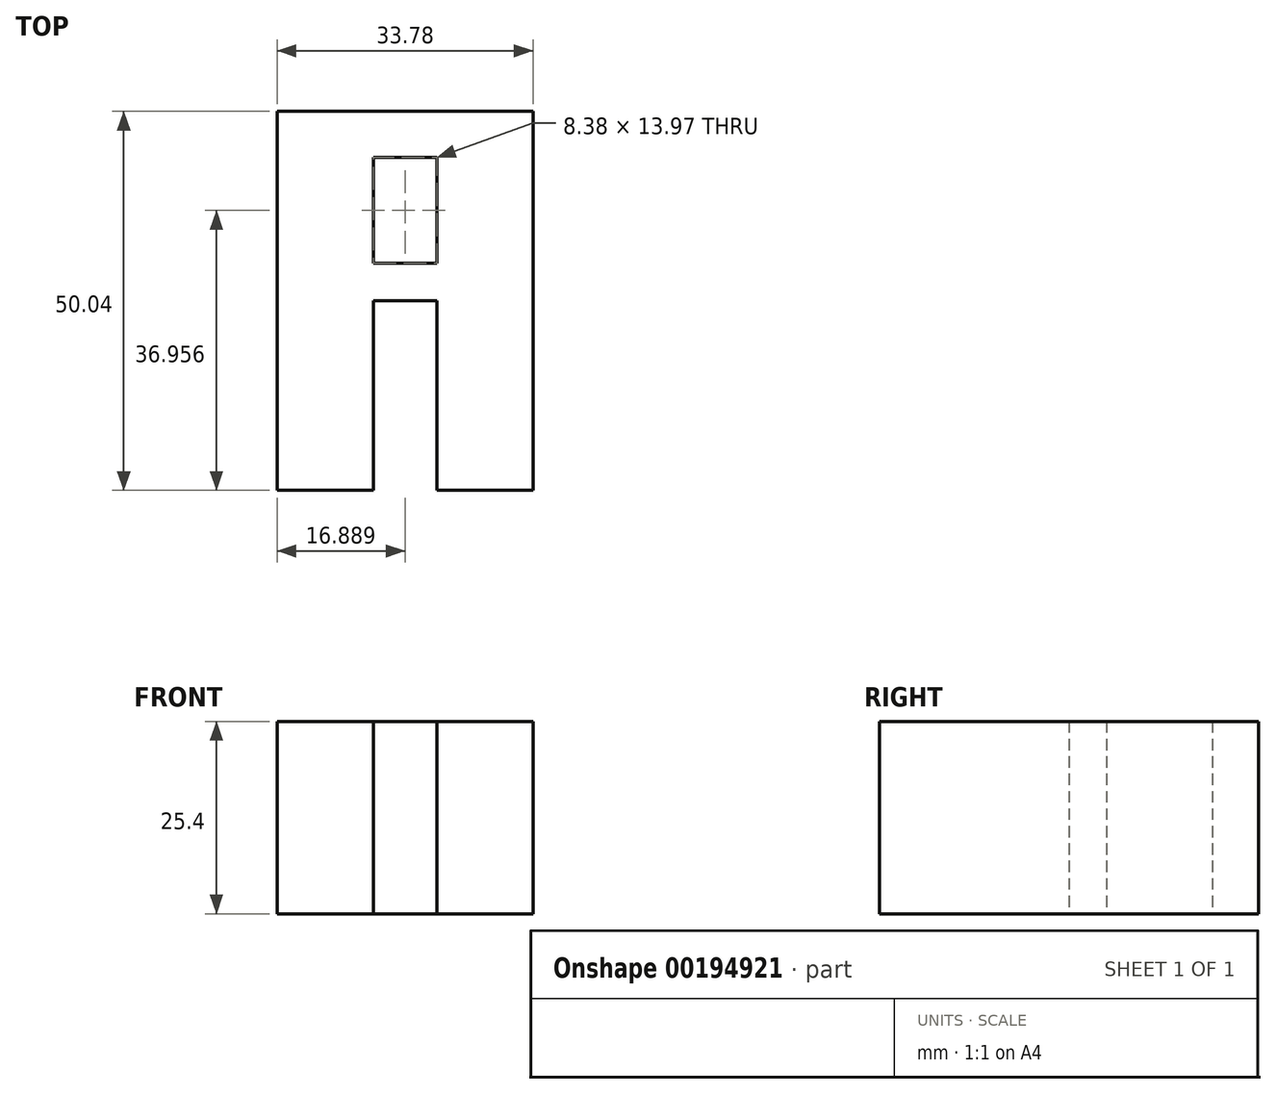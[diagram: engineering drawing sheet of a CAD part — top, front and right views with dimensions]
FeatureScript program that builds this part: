
annotation { "Feature Type Name" : "Feature", "Feature Type Description" : "" }
export const myFeature = defineFeature(function(context is Context, id is Id, definition is map)
    precondition{}
    {
        {
            var Q0;
            Q0=qCreatedBy(makeId("Top.planeOp"),FACE);
            var sketch = newSketch(context, id + "F0", { "sketchPlane" : qUnion([Q0])});
            skLineSegment(sketch, "E0.bottom", {"start": v(-24.9, 25.53) * mm, "end": v(-12.2, 25.53) * mm});
            skLineSegment(sketch, "E0.top", {"start": v(-24.9, -24.51) * mm, "end": v(-12.2, -24.51) * mm});
            skLineSegment(sketch, "E0.left", {"start": v(-24.9, 25.53) * mm, "end": v(-24.9, -24.51) * mm});
            skLineSegment(sketch, "E0.right", {"start": v(-12.2, 19.43) * mm, "end": v(-12.2, 5.46) * mm});
            skLineSegment(sketch, "E1.bottom", {"start": v(-24.9, 25.53) * mm, "end": v(8.89, 25.53) * mm});
            skLineSegment(sketch, "E1.top", {"start": v(-12.2, 19.43) * mm, "end": v(-3.81, 19.43) * mm});
            skLineSegment(sketch, "E1.left", {"start": v(-24.9, 25.53) * mm, "end": v(-24.9, 19.43) * mm});
            skLineSegment(sketch, "E1.right", {"start": v(8.89, 25.53) * mm, "end": v(8.89, 19.43) * mm});
            skLineSegment(sketch, "E2.bottom", {"start": v(8.89, 25.53) * mm, "end": v(-3.81, 25.53) * mm});
            skLineSegment(sketch, "E2.top", {"start": v(8.89, -24.51) * mm, "end": v(-3.81, -24.51) * mm});
            skLineSegment(sketch, "E2.left", {"start": v(8.89, 25.53) * mm, "end": v(8.89, -24.51) * mm});
            skLineSegment(sketch, "E2.right", {"start": v(-3.81, 19.43) * mm, "end": v(-3.81, 5.46) * mm});
            skPoint(sketch, "E3.startSnap0", {"position": v(-24.9, 0.5) * mm});
            skLineSegment(sketch, "E4.bottom", {"start": v(-12.2, 0.5) * mm, "end": v(-3.81, 0.5) * mm});
            skLineSegment(sketch, "E4.top", {"start": v(-12.2, 5.46) * mm, "end": v(-3.81, 5.46) * mm});
            skLineSegment(sketch, "E4.left", {"start": v(-24.9, 0.5) * mm, "end": v(-24.9, 5.46) * mm});
            skLineSegment(sketch, "E4.right", {"start": v(8.89, 0.5) * mm, "end": v(8.89, 5.46) * mm});
            skPoint(sketch, "E3.start.orphan", {"position": v(-24.9, 0) * mm});
            skLineSegment(sketch, "E5.trimOffspring", {"start": v(-12.2, 0.5) * mm, "end": v(-12.2, -24.51) * mm});
            skLineSegment(sketch, "E6.trimOffspring", {"start": v(-3.81, 0.5) * mm, "end": v(-3.81, -24.51) * mm});
            skSolve(sketch);
        }
        {
            var Q0;
            Q0 = qSketchRegion(id + "F0", true);
            extrude(context, id + "F1", {"entities" : qUnion([Q0]), "depth" : 25.4 * mm});
        }
    });
